# Revit family: Porecz_stała_dla_niepełnosprawnych_3-podporowa_prawa 550 mm
name_source: partatom
category: Furniture
units: mm (PartAtom-declared; Revit-internal decimal feet)

## family parameters
Always vertical = Yes
Cut with Voids When Loaded = No
Host = Wall
Room Calculation Point = No
Shared = No

## types (1)
- Type 1
    Depth / Glebokosc = 550 mm
    Description = Poręcz stała dla niepełnosprawnych 3-podporowa to uchwyt łazienkowy montowany po prawej stronie umywalek. Wykonany jest ze stali nierdzewnej matowej, a jego długość to 55 cm. Łatwy w montażu i czyszczeniu pochwyt dla niepełnosprawnych posiada trzy punkty podparcia, dzięki czemu jest bardzo mocny i stabilny. Umożliwia on podtrzymanie się osobom z dysfunkcjami ruchowymi  podczas wykonywana czynności w toalecie, co zwiększa ich samodzielność i bezpieczeństwo. Poręcze dla niepełnosprawnych doskonale sprawdzą się w szkołach, szpitalach, hotelach, czy domach opieki.
    Height / Wysokosc = 150 mm  [stored 0.492126 ft]
    Manufacturer = FANECO.com
    Manufacturer code / Kod producenta = 5901764295129
    Material = Stal nierdzewna polerowana
    Material finish / Wykonczenie = Materiał Stal nierdzewna AISI 316, mat
    Product code / Kod produktu = S32UUP55SNM
    Type Comments = Poręcz stała dla niepełnosprawnych 3-podporowa lewa 550 mm stal szlachetna matowa
    URL = https://faneco.com
    Weight / Waga = 1.9 kg
    Width / Szerokosc = 150 mm  [stored 0.492126 ft]

note: [stored X ft] marks values corroborated as IEEE doubles in the binary element streams (Revit-internal decimal feet)

## geometry (parser evidence)
native form markers: Sweep x11
no freeform markers — native parametric forms only
